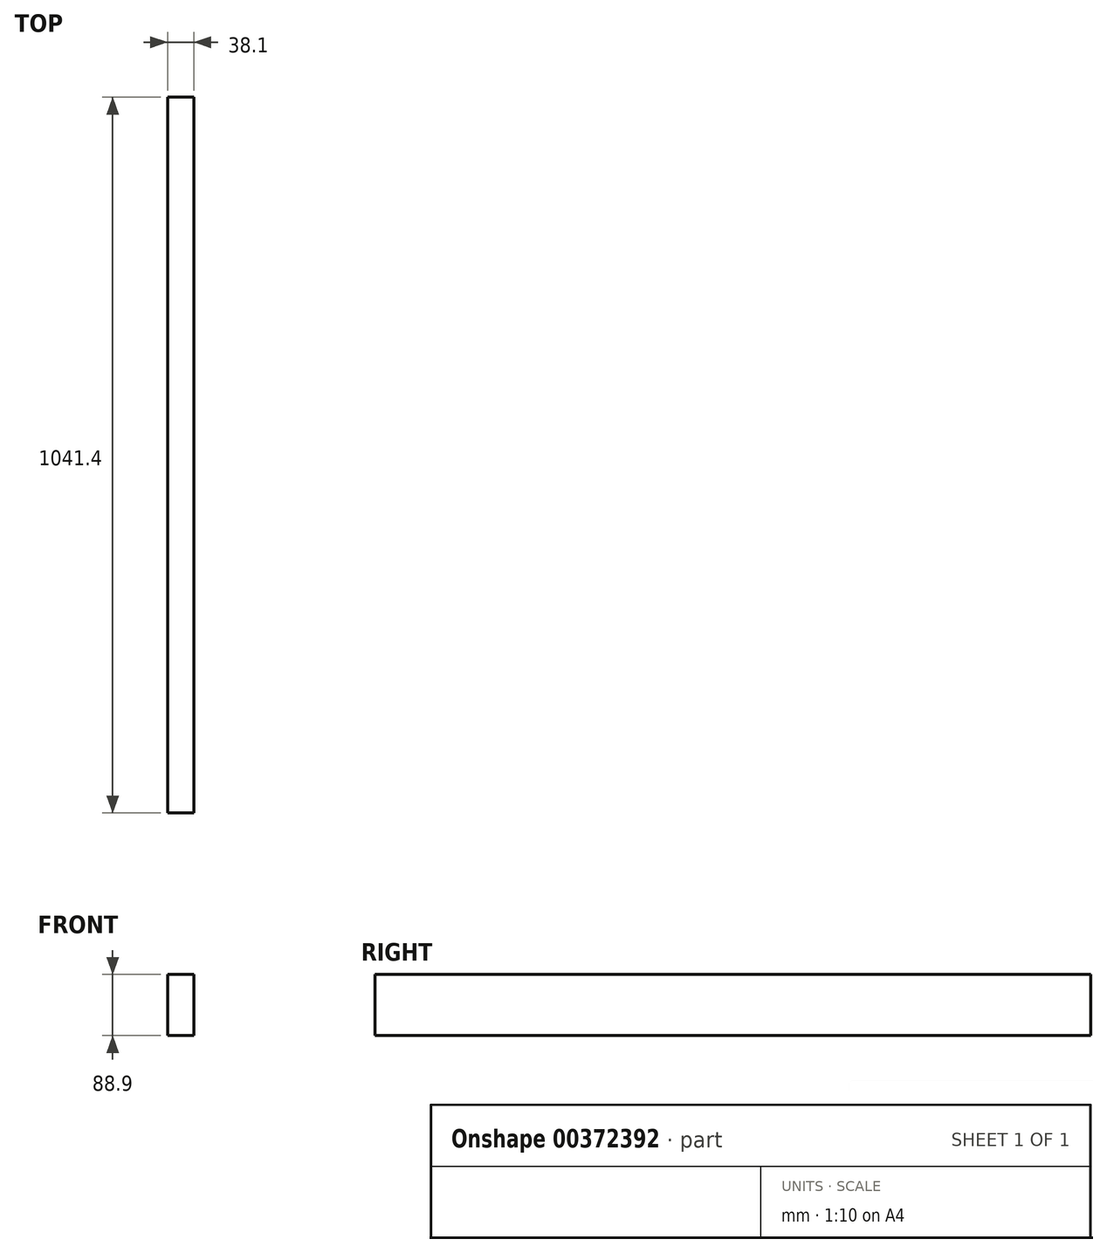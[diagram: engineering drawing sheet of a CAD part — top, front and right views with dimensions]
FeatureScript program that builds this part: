
annotation { "Feature Type Name" : "Feature", "Feature Type Description" : "" }
export const myFeature = defineFeature(function(context is Context, id is Id, definition is map)
    precondition{}
    {
        {
            var Q0;
            Q0=qCreatedBy(makeId("Front.planeOp"),FACE);
            var sketch = newSketch(context, id + "F0", { "sketchPlane" : qUnion([Q0])});
            skLineSegment(sketch, "E0.bottom", {"start": v(-19.05, 44.45) * mm, "end": v(19.05, 44.45) * mm});
            skLineSegment(sketch, "E0.top", {"start": v(-19.05, -44.45) * mm, "end": v(19.05, -44.45) * mm});
            skLineSegment(sketch, "E0.left", {"start": v(-19.05, 44.45) * mm, "end": v(-19.05, -44.45) * mm});
            skLineSegment(sketch, "E0.right", {"start": v(19.05, 44.45) * mm, "end": v(19.05, -44.45) * mm});
            skPoint(sketch, "E0.middle", {"position": v(0, 0) * mm});
            skSolve(sketch);
        }
        {
            var Q0;
            Q0=qSketchRegion(id+"F0",true);
            extrude(context, id + "F1", {"entities" : qUnion([Q0]), "endBound" : BoundingType.SYMMETRIC, "oppositeDirection" : true, "depth" : 1041.4 * mm});
        }
    });
